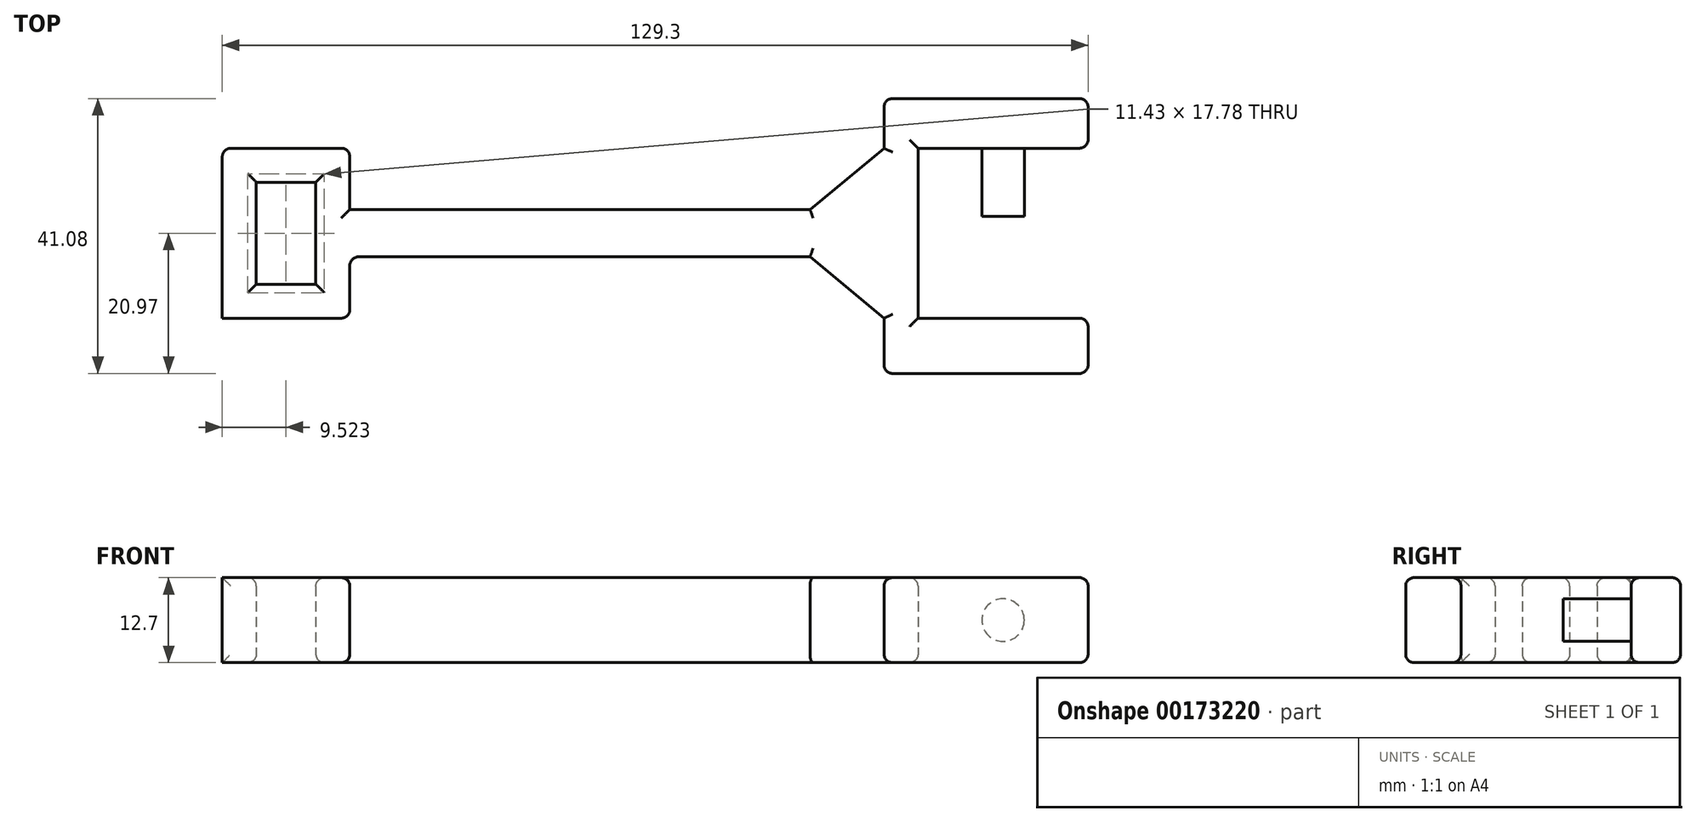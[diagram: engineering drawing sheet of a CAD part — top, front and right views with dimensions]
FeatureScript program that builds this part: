
annotation { "Feature Type Name" : "Feature", "Feature Type Description" : "" }
export const myFeature = defineFeature(function(context is Context, id is Id, definition is map)
    precondition{}
    {
        {
            var Q0;
            Q0=qCreatedBy(makeId("Top.planeOp"),FACE);
            var sketch = newSketch(context, id + "F0", { "sketchPlane" : qUnion([Q0])});
            skLineSegment(sketch, "E0.bottom", {"start": v(12.7, 12.7) * mm, "end": v(-12.7, 12.7) * mm});
            skLineSegment(sketch, "E0.top", {"start": v(12.7, -12.7) * mm, "end": v(-12.7, -12.7) * mm});
            skLineSegment(sketch, "E0.right", {"start": v(-12.7, 12.7) * mm, "end": v(-12.7, -12.7) * mm});
            skPoint(sketch, "E0.middle", {"position": v(0, 0) * mm});
            skLineSegment(sketch, "E1.top", {"start": v(12.7, 20.1) * mm, "end": v(-17.78, 20.1) * mm});
            skLineSegment(sketch, "E1.left", {"start": v(12.7, 12.7) * mm, "end": v(12.7, 20.1) * mm});
            skLineSegment(sketch, "E1.right", {"start": v(-17.78, 12.7) * mm, "end": v(-17.78, 20.1) * mm});
            skLineSegment(sketch, "E2.top", {"start": v(12.7, -20.97) * mm, "end": v(-17.78, -20.97) * mm});
            skLineSegment(sketch, "E2.left", {"start": v(12.7, -12.7) * mm, "end": v(12.7, -20.97) * mm});
            skLineSegment(sketch, "E2.right", {"start": v(-17.78, -12.7) * mm, "end": v(-17.78, -20.97) * mm});
            skLineSegment(sketch, "E3", {"start": v(-17.78, 12.7) * mm, "end": v(-28.83, 3.54) * mm});
            skLineSegment(sketch, "E4", {"start": v(-28.83, -3.54) * mm, "end": v(-17.78, -12.7) * mm});
            skLineSegment(sketch, "E5", {"start": v(-28.83, 3.54) * mm, "end": v(-97.55, 3.54) * mm});
            skLineSegment(sketch, "E6", {"start": v(-28.83, -3.54) * mm, "end": v(-97.55, -3.54) * mm});
            skLineSegment(sketch, "E7", {"start": v(-97.55, -3.54) * mm, "end": v(-97.55, -12.7) * mm});
            skLineSegment(sketch, "E8", {"start": v(-97.55, -12.7) * mm, "end": v(-116.6, -12.7) * mm});
            skLineSegment(sketch, "E9", {"start": v(-116.6, -12.7) * mm, "end": v(-116.6, 12.7) * mm});
            skLineSegment(sketch, "E10", {"start": v(-116.6, 12.7) * mm, "end": v(-97.55, 12.7) * mm});
            skLineSegment(sketch, "E11", {"start": v(-97.55, 12.7) * mm, "end": v(-97.55, 3.54) * mm});
            skPoint(sketch, "E12.orphan", {"position": v(-33.1, 0) * mm});
            skLineSegment(sketch, "E13.top", {"start": v(-116.6, -12.7) * mm, "end": v(-97.55, -12.7) * mm});
            skLineSegment(sketch, "E13.left", {"start": v(-116.6, 12.7) * mm, "end": v(-116.6, -12.7) * mm});
            skLineSegment(sketch, "E14.0", {"start": v(-111.52, 7.62) * mm, "end": v(-102.63, 7.62) * mm});
            skLineSegment(sketch, "E15.0", {"start": v(-111.52, 7.62) * mm, "end": v(-111.52, -7.62) * mm});
            skLineSegment(sketch, "E16.0", {"start": v(-102.63, -7.62) * mm, "end": v(-111.52, -7.62) * mm});
            skLineSegment(sketch, "E17.0", {"start": v(-102.63, 7.62) * mm, "end": v(-102.63, -7.62) * mm});
            skSolve(sketch);
        }
        {
            var Q0;
            Q0=makeQuery(id+"F0.imprint","IMPRINT",FACE,{"disambiguationData":[TD([[makeQuery(id+"F0.imprint","IMPRINT",EDGE,{"derivedFrom":sQuery(id+"F0.wireOp",EDGE,"E0.right")}),-1.0]])]});
            extrude(context, id + "F1", {"entities" : qUnion([Q0]), "depth" : 12.7 * mm});
        }
        {
            var Q0;
            Q0=makeQuery(id+"F1.opExtrude","SWEPT_FACE",FACE,{"disambiguationData":[OSD([sQuery(id+"F0.wireOp",EDGE,"E0.bottom")])]});
            var sketch = newSketch(context, id + "F2", { "sketchPlane" : qUnion([Q0])});
            skCircle(sketch, "E18", {"center": v(0, 6.35) * mm, "radius": 3.18 * mm});
            skPoint(sketch, "E18.centerSnap0", {"position": v(12.7, 6.35) * mm});
            skPoint(sketch, "E18.centerSnap1", {"position": v(0, 0) * mm});
            skSolve(sketch);
        }
        {
            var Q0;
            Q0=makeQuery(id+"F1.opExtrude","SWEPT_FACE",FACE,{"disambiguationData":[OSD([sQuery(id+"F0.wireOp",EDGE,"E0.top")])]});
            var sketch = newSketch(context, id + "F3", { "sketchPlane" : qUnion([Q0])});
            skCircle(sketch, "E19", {"center": v(0, 6.35) * mm, "radius": 3.18 * mm});
            skPoint(sketch, "E19.centerSnap0", {"position": v(-12.7, 6.35) * mm});
            skSolve(sketch);
        }
        {
            var Q0;
            Q0=sQuery(id+"F3.wireOp",EDGE,"E19");
            extrude(context, id + "F4", {"bodyType" : ToolBodyType.SURFACE, "surfaceEntities" : qUnion([Q0]), "depth" : 10.16 * mm});
        }
        {
            var Q0;
            Q0=makeQuery(id+"F2.imprint","IMPRINT",FACE,{"disambiguationData":[TD([[makeQuery(id+"F2.imprint","IMPRINT",EDGE,{"derivedFrom":sQuery(id+"F2.wireOp",EDGE,"E18")}),1.0]])]});
            extrude(context, id + "F5", {"entities" : qUnion([Q0]), "operationType" : NewBodyOperationType.ADD, "depth" : 10.16 * mm});
        }
        {
            var Q0;
            Q0=makeQuery(id+"F1.opExtrude","CAP_EDGE",EDGE,{"disambiguationData":[OSD([sQuery(id+"F0.wireOp",EDGE,"E6")])],"isStart":false});
            var Q1;
            Q1=makeQuery(id+"F1.opExtrude","CAP_EDGE",EDGE,{"disambiguationData":[OSD([sQuery(id+"F0.wireOp",EDGE,"E5")])],"isStart":false});
            var Q2;
            Q2=makeQuery(id+"F1.opExtrude","CAP_EDGE",EDGE,{"disambiguationData":[OSD([sQuery(id+"F0.wireOp",EDGE,"E6")])],"isStart":true});
            var Q3;
            Q3=makeQuery(id+"F1.opExtrude","CAP_EDGE",EDGE,{"disambiguationData":[OSD([sQuery(id+"F0.wireOp",EDGE,"E13.top")])],"isStart":false});
            var Q4;
            Q4=makeQuery(id+"F1.opExtrude","CAP_EDGE",EDGE,{"disambiguationData":[OSD([sQuery(id+"F0.wireOp",EDGE,"E7")])],"isStart":false});
            var Q5;
            Q5=makeQuery(id+"F1.opExtrude","SWEPT_EDGE",EDGE,{"disambiguationData":[OSD([sQuery(id+"F0.wireOp",EDGE,"E13.top"),sQuery(id+"F0.wireOp",EDGE,"E7")])]});
            var Q6;
            Q6=makeQuery(id+"F1.opExtrude","CAP_EDGE",EDGE,{"disambiguationData":[OSD([sQuery(id+"F0.wireOp",EDGE,"E7")])],"isStart":true});
            var Q7;
            Q7=makeQuery(id+"F1.opExtrude","CAP_EDGE",EDGE,{"disambiguationData":[OSD([sQuery(id+"F0.wireOp",EDGE,"E13.top")])],"isStart":true});
            var Q8;
            Q8=makeQuery(id+"F1.opExtrude","SWEPT_EDGE",EDGE,{"disambiguationData":[OSD([sQuery(id+"F0.wireOp",EDGE,"E13.top"),sQuery(id+"F0.wireOp",EDGE,"E13.left")])]});
            var Q9;
            Q9=makeQuery(id+"F1.opExtrude","CAP_EDGE",EDGE,{"disambiguationData":[OSD([sQuery(id+"F0.wireOp",EDGE,"E13.left")])],"isStart":false});
            var Q10;
            Q10=makeQuery(id+"F1.opExtrude","CAP_EDGE",EDGE,{"disambiguationData":[OSD([sQuery(id+"F0.wireOp",EDGE,"E10")])],"isStart":false});
            var Q11;
            Q11=makeQuery(id+"F1.opExtrude","CAP_EDGE",EDGE,{"disambiguationData":[OSD([sQuery(id+"F0.wireOp",EDGE,"E11")])],"isStart":false});
            var Q12;
            Q12=makeQuery(id+"F1.opExtrude","CAP_EDGE",EDGE,{"disambiguationData":[OSD([sQuery(id+"F0.wireOp",EDGE,"E17.0")])],"isStart":false});
            var Q13;
            Q13=makeQuery(id+"F1.opExtrude","CAP_EDGE",EDGE,{"disambiguationData":[OSD([sQuery(id+"F0.wireOp",EDGE,"E14.0")])],"isStart":false});
            var Q14;
            Q14=makeQuery(id+"F1.opExtrude","CAP_EDGE",EDGE,{"disambiguationData":[OSD([sQuery(id+"F0.wireOp",EDGE,"E15.0")])],"isStart":false});
            var Q15;
            Q15=makeQuery(id+"F1.opExtrude","CAP_EDGE",EDGE,{"disambiguationData":[OSD([sQuery(id+"F0.wireOp",EDGE,"E16.0")])],"isStart":false});
            var Q16;
            Q16=makeQuery(id+"F1.opExtrude","SWEPT_EDGE",EDGE,{"disambiguationData":[OSD([sQuery(id+"F0.wireOp",EDGE,"E10"),sQuery(id+"F0.wireOp",EDGE,"E13.left")])]});
            var Q17;
            Q17=makeQuery(id+"F1.opExtrude","CAP_EDGE",EDGE,{"disambiguationData":[OSD([sQuery(id+"F0.wireOp",EDGE,"E13.left")])],"isStart":true});
            var Q18;
            Q18=makeQuery(id+"F1.opExtrude","CAP_EDGE",EDGE,{"disambiguationData":[OSD([sQuery(id+"F0.wireOp",EDGE,"E15.0")])],"isStart":true});
            var Q19;
            Q19=makeQuery(id+"F1.opExtrude","CAP_EDGE",EDGE,{"disambiguationData":[OSD([sQuery(id+"F0.wireOp",EDGE,"E14.0")])],"isStart":true});
            var Q20;
            Q20=makeQuery(id+"F1.opExtrude","CAP_EDGE",EDGE,{"disambiguationData":[OSD([sQuery(id+"F0.wireOp",EDGE,"E17.0")])],"isStart":true});
            var Q21;
            Q21=makeQuery(id+"F1.opExtrude","CAP_EDGE",EDGE,{"disambiguationData":[OSD([sQuery(id+"F0.wireOp",EDGE,"E16.0")])],"isStart":true});
            var Q22;
            Q22=makeQuery(id+"F1.opExtrude","CAP_EDGE",EDGE,{"disambiguationData":[OSD([sQuery(id+"F0.wireOp",EDGE,"E10")])],"isStart":true});
            var Q23;
            Q23=makeQuery(id+"F1.opExtrude","SWEPT_EDGE",EDGE,{"disambiguationData":[OSD([sQuery(id+"F0.wireOp",EDGE,"E10"),sQuery(id+"F0.wireOp",EDGE,"E11")])]});
            var Q24;
            Q24=makeQuery(id+"F1.opExtrude","CAP_EDGE",EDGE,{"disambiguationData":[OSD([sQuery(id+"F0.wireOp",EDGE,"E11")])],"isStart":true});
            var Q25;
            Q25=makeQuery(id+"F1.opExtrude","CAP_EDGE",EDGE,{"disambiguationData":[OSD([sQuery(id+"F0.wireOp",EDGE,"E5")])],"isStart":true});
            var Q26;
            Q26=makeQuery(id+"F1.opExtrude","SWEPT_EDGE",EDGE,{"disambiguationData":[OSD([sQuery(id+"F0.wireOp",EDGE,"E1.top"),sQuery(id+"F0.wireOp",EDGE,"E1.right")])]});
            var Q27;
            Q27=makeQuery(id+"F1.opExtrude","CAP_EDGE",EDGE,{"disambiguationData":[OSD([sQuery(id+"F0.wireOp",EDGE,"E3")])],"isStart":false});
            var Q28;
            Q28=makeQuery(id+"F1.opExtrude","CAP_EDGE",EDGE,{"disambiguationData":[OSD([sQuery(id+"F0.wireOp",EDGE,"E3")])],"isStart":true});
            var Q29;
            Q29=makeQuery(id+"F1.opExtrude","CAP_EDGE",EDGE,{"disambiguationData":[OSD([sQuery(id+"F0.wireOp",EDGE,"E1.right")])],"isStart":true});
            var Q30;
            Q30=makeQuery(id+"F1.opExtrude","CAP_EDGE",EDGE,{"disambiguationData":[OSD([sQuery(id+"F0.wireOp",EDGE,"E1.right")])],"isStart":false});
            var Q31;
            Q31=makeQuery(id+"F1.opExtrude","CAP_EDGE",EDGE,{"disambiguationData":[OSD([sQuery(id+"F0.wireOp",EDGE,"E1.top")])],"isStart":false});
            var Q32;
            Q32=makeQuery(id+"F1.opExtrude","CAP_EDGE",EDGE,{"disambiguationData":[OSD([sQuery(id+"F0.wireOp",EDGE,"E1.top")])],"isStart":true});
            var Q33;
            Q33=makeQuery(id+"F1.opExtrude","CAP_EDGE",EDGE,{"disambiguationData":[OSD([sQuery(id+"F0.wireOp",EDGE,"E0.bottom")])],"isStart":true});
            var Q34;
            Q34=makeQuery(id+"F1.opExtrude","CAP_EDGE",EDGE,{"disambiguationData":[OSD([sQuery(id+"F0.wireOp",EDGE,"E1.left")])],"isStart":true});
            var Q35;
            Q35=makeQuery(id+"F1.opExtrude","SWEPT_EDGE",EDGE,{"disambiguationData":[OSD([sQuery(id+"F0.wireOp",EDGE,"E1.top"),sQuery(id+"F0.wireOp",EDGE,"E1.left")])]});
            var Q36;
            Q36=makeQuery(id+"F1.opExtrude","SWEPT_EDGE",EDGE,{"disambiguationData":[OSD([sQuery(id+"F0.wireOp",EDGE,"E0.top"),sQuery(id+"F0.wireOp",EDGE,"E2.left")])]});
            var Q37;
            Q37=makeQuery(id+"F1.opExtrude","CAP_EDGE",EDGE,{"disambiguationData":[OSD([sQuery(id+"F0.wireOp",EDGE,"E0.top")])],"isStart":true});
            var Q38;
            Q38=makeQuery(id+"F1.opExtrude","CAP_EDGE",EDGE,{"disambiguationData":[OSD([sQuery(id+"F0.wireOp",EDGE,"E2.left")])],"isStart":true});
            var Q39;
            Q39=makeQuery(id+"F1.opExtrude","CAP_EDGE",EDGE,{"disambiguationData":[OSD([sQuery(id+"F0.wireOp",EDGE,"E2.top")])],"isStart":true});
            var Q40;
            Q40=makeQuery(id+"F1.opExtrude","CAP_EDGE",EDGE,{"disambiguationData":[OSD([sQuery(id+"F0.wireOp",EDGE,"E2.right")])],"isStart":true});
            var Q41;
            Q41=makeQuery(id+"F1.opExtrude","CAP_EDGE",EDGE,{"disambiguationData":[OSD([sQuery(id+"F0.wireOp",EDGE,"E0.right")])],"isStart":true});
            var Q42;
            Q42=makeQuery(id+"F1.opExtrude","CAP_EDGE",EDGE,{"disambiguationData":[OSD([sQuery(id+"F0.wireOp",EDGE,"E4")])],"isStart":true});
            var Q43;
            Q43=makeQuery(id+"F1.opExtrude","CAP_EDGE",EDGE,{"disambiguationData":[OSD([sQuery(id+"F0.wireOp",EDGE,"E4")])],"isStart":false});
            var Q44;
            Q44=makeQuery(id+"F1.opExtrude","CAP_EDGE",EDGE,{"disambiguationData":[OSD([sQuery(id+"F0.wireOp",EDGE,"E0.right")])],"isStart":false});
            var Q45;
            Q45=makeQuery(id+"F1.opExtrude","CAP_EDGE",EDGE,{"disambiguationData":[OSD([sQuery(id+"F0.wireOp",EDGE,"E0.bottom")])],"isStart":false});
            var Q46;
            Q46=makeQuery(id+"F1.opExtrude","CAP_EDGE",EDGE,{"disambiguationData":[OSD([sQuery(id+"F0.wireOp",EDGE,"E1.left")])],"isStart":false});
            var Q47;
            Q47=makeQuery(id+"F1.opExtrude","SWEPT_EDGE",EDGE,{"disambiguationData":[OSD([sQuery(id+"F0.wireOp",EDGE,"E0.bottom"),sQuery(id+"F0.wireOp",EDGE,"E1.left")])]});
            var Q48;
            Q48=makeQuery(id+"F1.opExtrude","CAP_EDGE",EDGE,{"disambiguationData":[OSD([sQuery(id+"F0.wireOp",EDGE,"E2.right")])],"isStart":false});
            var Q49;
            Q49=makeQuery(id+"F1.opExtrude","SWEPT_EDGE",EDGE,{"disambiguationData":[OSD([sQuery(id+"F0.wireOp",EDGE,"E2.top"),sQuery(id+"F0.wireOp",EDGE,"E2.right")])]});
            var Q50;
            Q50=makeQuery(id+"F1.opExtrude","CAP_EDGE",EDGE,{"disambiguationData":[OSD([sQuery(id+"F0.wireOp",EDGE,"E2.top")])],"isStart":false});
            var Q51;
            Q51=makeQuery(id+"F1.opExtrude","CAP_EDGE",EDGE,{"disambiguationData":[OSD([sQuery(id+"F0.wireOp",EDGE,"E0.top")])],"isStart":false});
            var Q52;
            Q52=makeQuery(id+"F1.opExtrude","CAP_EDGE",EDGE,{"disambiguationData":[OSD([sQuery(id+"F0.wireOp",EDGE,"E2.left")])],"isStart":false});
            var Q53;
            Q53=makeQuery(id+"F1.opExtrude","SWEPT_EDGE",EDGE,{"disambiguationData":[OSD([sQuery(id+"F0.wireOp",EDGE,"E2.top"),sQuery(id+"F0.wireOp",EDGE,"E2.left")])]});
            fillet(context, id + "F6", {"entities" : qUnion([Q0, Q1, Q2, Q3, Q4, Q5, Q6, Q7, Q8, Q9, Q10, Q11, Q12, Q13, Q14, Q15, Q16, Q17, Q18, Q19, Q20, Q21, Q22, Q23, Q24, Q25, Q26, Q27, Q28, Q29, Q30, Q31, Q32, Q33, Q34, Q35, Q36, Q37, Q38, Q39, Q40, Q41, Q42, Q43, Q44, Q45, Q46, Q47, Q48, Q49, Q50, Q51, Q52, Q53]), "radius" : 1.27 * mm, "tangentPropagation" : true, "allowEdgeOverflow" : false});
        }
    });
